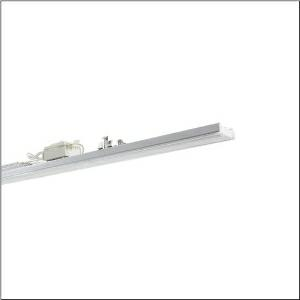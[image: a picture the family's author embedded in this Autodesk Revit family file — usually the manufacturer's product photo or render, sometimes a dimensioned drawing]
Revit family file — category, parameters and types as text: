
# Revit family: licross_21_recessed_ho_52tl12dv4l2m3s
name_source: partatom
category: Lighting Fixtures
units: mm (PartAtom-declared; Revit-internal decimal feet)

## family parameters
Cut with Voids When Loaded = No
Host = Face
Light Source = No
Part Type = Normal
Room Calculation Point = No
Round Connector Dimension = Use Diameter
Shared = No

## types (1)
- --- (1 x LED, 910 lm, 6.4 W, 4000K)
    Apparent Load = 6 VA
    CIE Flux Codes = 69 91 98 100 100
    Color Rendering = 80
    Color Temperature = 4000K
    Default Elevation = 1800 mm
    Description = Licross 21 Recessed HO, luminaire insert, of sheet steel, galvanised, coil coated, white, length: 2.250mm, width: 66mm, height: 67mm, LED rated luminous flux: 22.710lm, light colour: 840, SDCM (Standard Deviation of Colour Matching)MacAdam ≤ 3 SDCM (initial), control gear: DALI 2 (for two DALI lines), with plug, 6-pole, with phase selection, for trunking rail, 14-core, mains connection: 220..240V, AC, 50/60Hz, rated input power: 129W, for trunking rail, 14-core, internal wiring halogen-free, for emergency light function, converter,control gear: single battery element, battery: LiFePO4, 9Ah, primary optical cover: cover, of PMMA, light emission: direct distribution, primary light characteristic: symmetric, protection rating (complete): IP40, insulation class (complete): insulation class I (protective earthing), certification: CE, UKCA, protection symbol: D if used in an environment without relevant dust loads with corresponding accessories, impact resistance: IK06, permissible ambient temperature for indoor applications: +5..+30°C, standard: EN 60598-2-22, LABS conformity tested according to VDMA 24364:2018-05, reducing of maximum allowable ambient temperature of 5°C with ceiling mounting, corresponds to IFS (International Featured Standards) requirements for safety and quality in the food industry, The light source and the operating device comply with the requirements of the Ecodesign Regulation (EU) 2019/2020 and are replaceable in accordance with this regulation, packaging unit: 1 piece
    Height = 58 mm
    Lamp = 1 x LED
    Lamp Light Flux = 910 lm
    Lamp Power = 6.4 W
    Lamp count = 1
    Length = 2250 mm
    Luminous efficacy = 142 lm/W
    Manufacturer = Siteco
    ModVariant = No
    Model = 52TL12DV4L2M3S
    Mounting Place = Ceiling
    Mounting Type = Pendant
    Number of Poles = 1
    OnlyDefault = Yes
    Power Factor = 1
    Product Name = Licross 21 Recessed HO
    Product group = luminaire insert | ceiling pendant
    ProductGroupID = 901
    Protection Class = Protection class I
    Protection Degree = IP 40
    RLX_Detail_Level = 1
    RLX_Emergency_Light_Flux = 0 lm
    RLX_Emergency_Type = 0
    RLX_Emergency_Type_DB = No
    RlxData = <blob elided: 30245 chars, md5=37d7387c>
    Socket = socket
    Standby Power = 0 W
    System Light Flux = 910 lm
    System Power = 6 W
    Type Comments = : emergency light operation: 3 h
    Type Image = l_1296930.jpg
    URL = http://relux.com
    VarID = @adj_109239
    Voltage = 0 V
    Weight = 0.00 kg
    Width = 66 mm

## geometry (parser evidence)
native form markers: Blend x4, Sweep x9
no freeform markers — native parametric forms only
